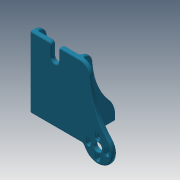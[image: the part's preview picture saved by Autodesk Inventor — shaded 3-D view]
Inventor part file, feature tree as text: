
AUTODESK INVENTOR PART (.ipt)
format: ipt  version: 2014 (Build 180170000, 170)  size: 877,568 bytes
history: native  units: mm
features: fillet x12, extrude x9, sketch x8, mirror x1
ambient origin geometry x8: Origin, YZ Plane, XZ Plane, XY Plane, X Axis, Y Axis, Z Axis, Center Point
bodies: Solid1 (feature_tree)
feature tree (30):
  extrude  "Extrusion1"  Depth=41.0mm
  extrude  "Extrusion2"  Depth=45.0mm
  extrude  "Extrusion3"  Depth=7.0mm TaperAngle=0.0deg
  mirror  "Mirror1"
  sketch  "Sketch4"  dims[d4=4.8mm d5=7.0mm d6=0.0mm]
  extrude  "Extrusion5"  Depth=10.0mm TaperAngle=0.0deg
  extrude  "Extrusion6"  Depth=12.0mm
  extrude  "Extrusion7"  Depth=25.0mm
  extrude  "Extrusion8"  Depth=2.0mm TaperAngle=0.0deg
  extrude  "Extrusion9"  Depth=2.0mm
  extrude  "Extrusion10"  Depth=2.0mm
  fillet  "Fillet1"  Radius=3.5mm
  fillet  "Fillet2"  Radius=4.5mm
  fillet  "Fillet3"  Radius=2.5mm
  fillet  "Fillet5"  Radius=2.5mm
  fillet  "Fillet6"  Radius=6.0mm
  fillet  "Fillet7"  Radius=7.0mm
  fillet  "Fillet8"  Radius=6.0mm
  fillet  "Fillet9"  Radius=15.0mm
  fillet  "Fillet10"  Radius=15.0mm
  fillet  "Fillet11"  Radius=6.0mm
  fillet  "Fillet12"  Radius=6.0mm
  fillet  "Fillet13"  Radius=6.0mm
  sketch  "Sketch1"  dims[d0=26.0mm d1=41.0mm]
  sketch  "Sketch2"  dims[d2=70.0mm d3=45.0mm]
  sketch  "Sketch5"  dims[d7=10.0mm d10=6.0mm d11=0.0mm]
  sketch  "Sketch6"  dims[d12=6.0mm d13=0.0mm d14=12.0mm]
  sketch  "Sketch7"  dims[d15=15.0mm d17=25.0mm]
  sketch  "Sketch8"  dims[d20=10.75mm d21=2.0mm d22=0.0mm]
  sketch  "Sketch9"  dims[d23=6.0mm d24=13.0mm d25=13.0mm d26=3.5mm d27=4.5mm d28=2.5mm d29=2.5mm d30=6.0mm d31=0.0mm d32=7.0mm d33=0.0mm d34=6.0mm d35=15.0mm d36=15.0mm d37=6.0mm d38=6.0mm d39=6.0mm d40=10.0mm d41=6.0mm d42=2.0mm d43=0.0mm d44=5.75mm d45=2.5mm d46=0.0mm d47=4.0mm d48=2.0mm d49=2.0mm d51=2.0mm d52=2.0mm d53=2.0mm d54=2.0mm d55=1.0mm d56=2.0mm d57=0.75mm d58=30.0mm d59=45.0mm d60=15.0mm d61=6.0mm d62=0.0mm d63=2.0mm d64=2.0mm d65=82.5mm d66=100.0mm d67=60.0mm]
